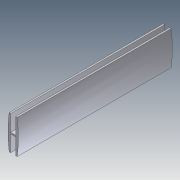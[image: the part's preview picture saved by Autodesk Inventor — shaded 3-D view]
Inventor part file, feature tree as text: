
AUTODESK INVENTOR PART (.ipt)
format: ipt  version: 2012 (Build 160160000, 160)  size: 91,136 bytes
history: native  units: in
note: dims shown in document units (in); Inventor stores cm internally (conversion verified against a paired STEP export)
features: extrude x1, sketch x1
ambient origin geometry x8: Origin, YZ Plane, XZ Plane, XY Plane, X Axis, Y Axis, Z Axis, Center Point
bodies: Solid1 (feature_tree)
feature tree (2):
  extrude  "Extrusion1"  Depth=0.0781in
  sketch  "Sketch1"  dims[d0=0.5234in d1=1.0469in d2=0.0781in d3=0.1562in d4=0.0781in d5=0.1562in d6=0.0234in d7=0.0469in d8=0.5234in d9=1.0469in d10=4.0in d12=0.0469in d13=4.75in d14=0.0in]
